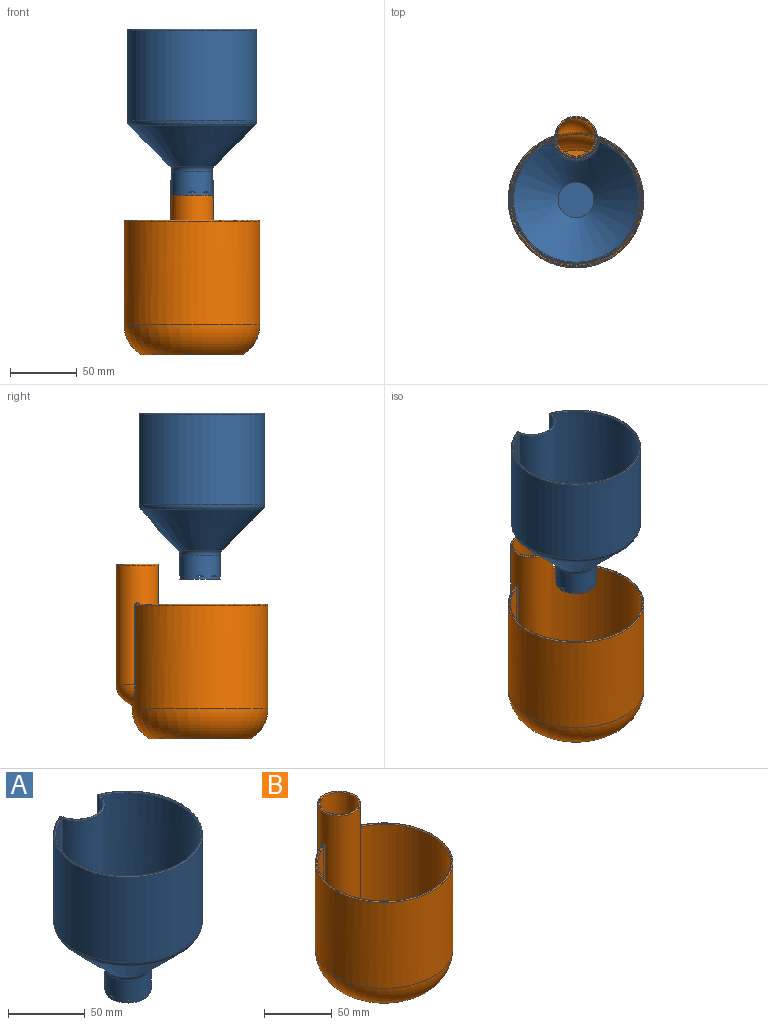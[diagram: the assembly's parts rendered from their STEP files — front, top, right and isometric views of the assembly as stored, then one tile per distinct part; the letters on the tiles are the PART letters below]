
ASSEMBLY  parts=2 mates=1
PART A: 33 faces, bbox 104.9x101.7x124.2 mm
  f0: cylinder r=15mm len=30mm, axis (0,0,1), area 1658.7mm2, adj f7,f8,f11,f12,f13,f14,f15,f16
  f1: cylinder r=13.4mm len=26.8mm, axis (0,0,1), area 1573.9mm2, adj f6,f8,f11,f12,f13,f14,f15,f16
  f2: plane 95.4x92.13mm, normal (0,0,1), area 33.3mm2, adj f23,f24,f25,f26,f27,f28,f29,f30
  f3: cylinder r=48.45mm len=96.9mm, axis (0,0,1), area 18219.3mm2, adj f19,f20,f23,f31
  f4: cone r=48.45mm half-angle=45deg, axis (0,0,1), area 8042mm2, adj f10,f31,f32
  f5: cylinder r=46.85mm len=93.7mm, axis (0,0,1), area 17716mm2, adj f6,f21,f22,f27
  f6: cone r=47.32mm half-angle=45deg, axis (0,0,1), area 8289.4mm2, adj f1,f5,f9,f21,f22
  f7: plane 30x30mm, normal (0,0,-1), area 706.9mm2, adj f0
  f8: plane 30x30mm, normal (0,0,1), area 629.7mm2, adj f0,f1,f11,f12,f13,f14,f15,f16
  f9: cylinder r=18.15mm len=87.34mm, axis (0,0,-1), area 3828.6mm2, adj f6,f21,f22,f30
  f10: cylinder r=16.55mm len=88mm, axis (0,0,-1), area 3801mm2, adj f4,f19,f20,f26,f31
  f11: cylinder r=3.5mm len=5.1mm, axis (0,1,0), area 9.2mm2, adj f0,f1,f8
  f12: cylinder r=3.5mm len=4.91mm, axis (0.71,0.71,0), area 9.2mm2, adj f0,f1,f8
  f13: cylinder r=3.5mm len=5.1mm, axis (1,0,0), area 9.2mm2, adj f0,f1,f8
  f14: cylinder r=3.5mm len=4.91mm, axis (0.71,-0.71,0), area 9.2mm2, adj f0,f1,f8
  f15: cylinder r=3.5mm len=5.1mm, axis (0,-1,0), area 9.2mm2, adj f0,f1,f8
  f16: cylinder r=3.5mm len=4.91mm, axis (0.71,-0.71,0), area 9.2mm2, adj f0,f1,f8
  f17: cylinder r=3.5mm len=4.91mm, axis (-0.71,-0.71,0), area 9.2mm2, adj f0,f1,f8
  f18: cylinder r=3.5mm len=5.1mm, axis (-1,0,0), area 9.2mm2, adj f0,f1,f8
  f19: cylinder r=1mm len=71.18mm, axis (0,0,-1), area 124.3mm2, adj f3,f10,f24,f31
  f20: cylinder r=1mm len=71.18mm, axis (0,0,1), area 124.3mm2, adj f3,f10,f25,f31
  f21: cylinder r=1mm len=70.47mm, axis (0,0,-1), area 119.9mm2, adj f5,f6,f9,f28
  f22: cylinder r=1mm len=70.47mm, axis (0,0,1), area 119.9mm2, adj f5,f6,f9,f29
  f23: torus R=47.7mm, axis (0,0,-1), area 314.2mm2, adj f2,f3,f24,f25
  f24: torus R=0.25mm, axis (0,0,-1), area 1.5mm2, adj f2,f19,f23,f26
  f25: torus R=0.25mm, axis (0,0,-1), area 1.5mm2, adj f2,f20,f23,f26
  f26: torus R=17.3mm, axis (0,0,-1), area 55.9mm2, adj f2,f10,f24,f25
  f27: torus R=47.6mm, axis (0,0,-1), area 302.8mm2, adj f2,f5,f28,f29
  f28: torus R=1.75mm, axis (0,0,-1), area 2.6mm2, adj f2,f21,f27,f30
  f29: torus R=1.75mm, axis (0,0,-1), area 2.6mm2, adj f2,f22,f27,f30
  f30: torus R=17.4mm, axis (0,0,-1), area 55mm2, adj f2,f9,f28,f29
  f31: torus R=43.45mm, axis (0,0,-1), area 1047.8mm2, adj f3,f4,f10,f19,f20
  f32: torus R=20mm, axis (0,0,1), area 382.4mm2, adj f0,f4
PART B: 34 faces, bbox 110.4x119.5x132.9 mm
  f0: cylinder r=15.8mm len=128.45mm, axis (0,0,1), area 9906.8mm2, adj f4,f9,f15,f17,f21,f22,f23,f24
  f1: cylinder r=14.2mm len=128.45mm, axis (0,0,1), area 9396.6mm2, adj f2,f5,f13,f14,f20,f22,f33
  f2: cylinder r=49.2mm len=28.4mm, axis (0,0,1), area 153.3mm2, adj f1,f14,f33
  f3: plane 30.1x30.1mm, normal (0,0,1), area 9.4mm2, adj f20,f21
  f4: sphere r=15.8mm, area 623.2mm2, adj f0,f16
  f5: sphere r=14.2mm, area 519.3mm2, adj f1,f33
  f6: cylinder r=50.8mm len=101.6mm, axis (0,0,1), area 22375.1mm2, adj f7,f15,f16,f17,f18
  f7: torus R=25mm, axis (0,0,1), area 7917.2mm2, adj f6,f8
  f8: plane 75.43x75.43mm, normal (0,0,-1), area 4468.1mm2, adj f7
  f9: plane 74.96x73.08mm, normal (0,0,1), area 4275.3mm2, adj f0,f12,f23,f28
  f10: plane 100.1x97.2mm, normal (0,0,1), area 28mm2, adj f18,f19,f26,f31
  f11: cylinder r=49.2mm len=98.4mm, axis (0,0,1), area 21286.1mm2, adj f12,f19,f24,f29
  f12: torus R=25mm, axis (0,0,1), area 6308.3mm2, adj f9,f11,f23,f28
  f13: plane 18.3x4.48mm, normal (0,0,1), area 55.8mm2, adj f1,f14
  f14: torus R=25mm, axis (0,0,1), area 671.4mm2, adj f1,f2,f13
  f15: cylinder r=1mm len=59.25mm, axis (0,0,-1), area 66.4mm2, adj f0,f6,f16,f32
  f16: bspline ~32.71x17.84mm, area 60mm2, adj f4,f6,f15,f17
  f17: cylinder r=1mm len=59.25mm, axis (0,0,1), area 66.4mm2, adj f0,f6,f16,f27
  f18: torus R=50.05mm, axis (0,0,-1), area 334.1mm2, adj f6,f10,f27,f32
  f19: torus R=49.95mm, axis (0,0,-1), area 325.6mm2, adj f10,f11,f25,f30
  f20: torus R=14.95mm, axis (0,0,-1), area 107.1mm2, adj f1,f3
  f21: torus R=15.05mm, axis (0,0,-1), area 114.9mm2, adj f0,f3
  f22: cylinder r=7.5mm len=15mm, axis (0,-1,0), area 80.9mm2, adj f0,f1
  f23: bspline ~23.97x13.74mm, area 41.2mm2, adj f0,f9,f12,f24
  f24: cylinder r=1mm len=77.6mm, axis (0,0,1), area 141.1mm2, adj f0,f11,f23,f25
  f25: bspline ~2.14x2.13mm, area 3mm2, adj f0,f19,f24,f26
  f26: torus R=16.8mm, axis (0,0,-1), area 0.2mm2, adj f0,f10,f25,f27
  f27: bspline ~2.05x1.99mm, area 2.5mm2, adj f0,f17,f18,f26
  f28: bspline ~23.97x13.74mm, area 41.2mm2, adj f0,f9,f12,f29
  f29: cylinder r=1mm len=77.6mm, axis (0,0,-1), area 141.1mm2, adj f0,f11,f28,f30
  f30: bspline ~2.14x2.13mm, area 3mm2, adj f0,f19,f29,f31
  f31: torus R=16.8mm, axis (0,0,-1), area 0.2mm2, adj f0,f10,f30,f32
  f32: bspline ~1.88x1.87mm, area 2.5mm2, adj f0,f15,f18,f31
  f33: bspline ~30.99x16.56mm, area 99.3mm2, adj f1,f2,f5
PLACE A t=(0,0,118.08)mm
PLACE B at identity fixed
MATE slider A.f0 <-> B.f6  axis (0,0,-1) through (0,0,118.88)mm
